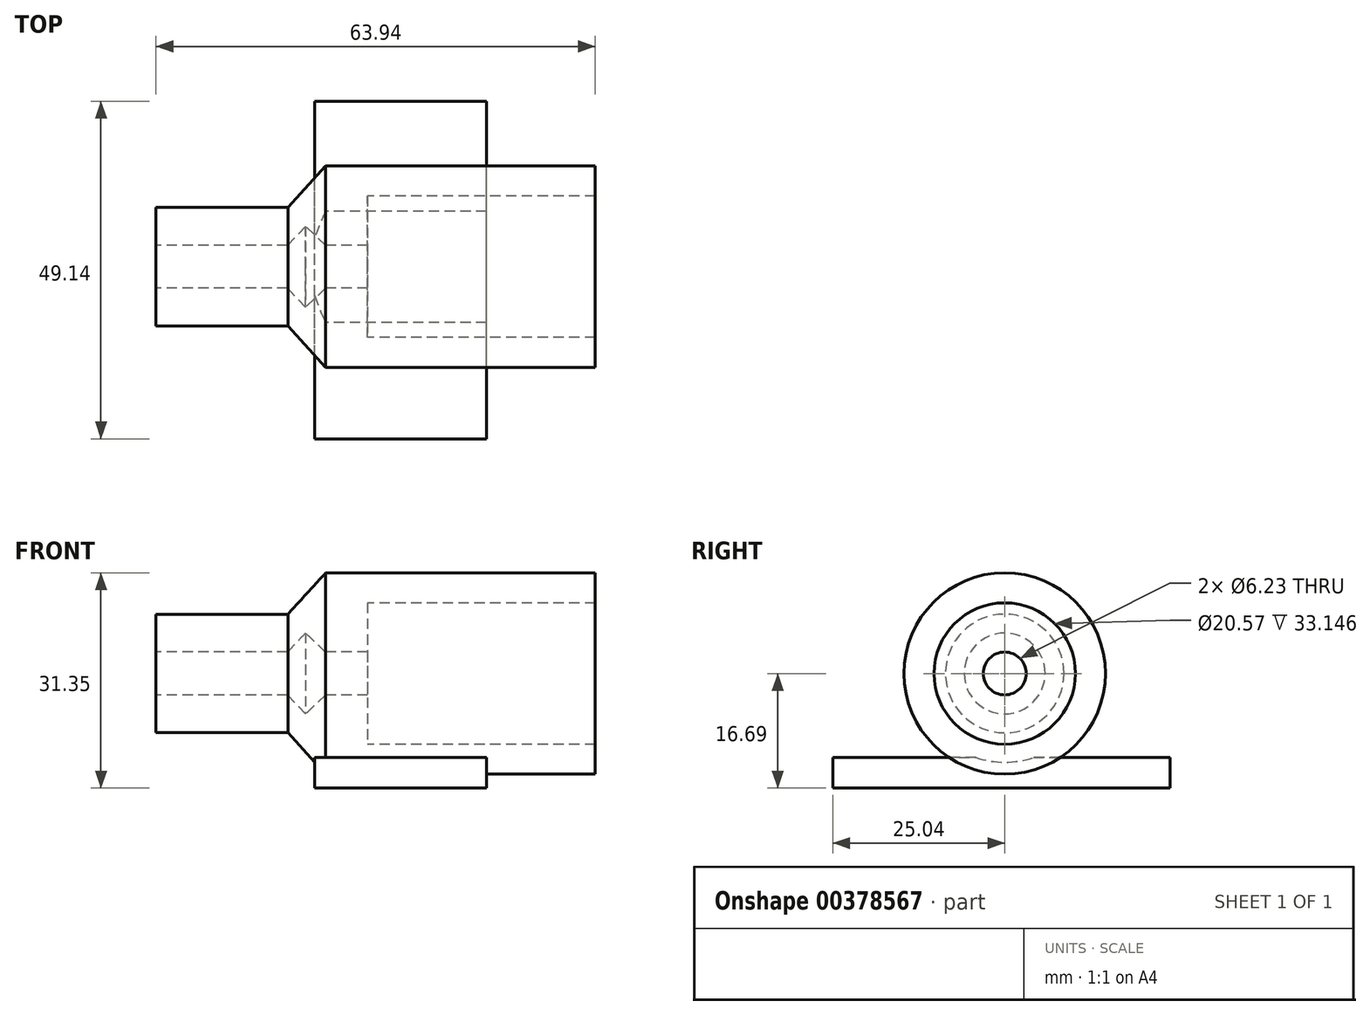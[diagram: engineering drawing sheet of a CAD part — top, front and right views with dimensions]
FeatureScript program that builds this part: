
annotation { "Feature Type Name" : "Feature", "Feature Type Description" : "" }
export const myFeature = defineFeature(function(context is Context, id is Id, definition is map)
    precondition{}
    {
        {
            var Q0;
            Q0=qCreatedBy(makeId("Top.planeOp"),FACE);
            var sketch = newSketch(context, id + "F0", { "sketchPlane" : qUnion([Q0])});
            skLineSegment(sketch, "E0", {"start": v(-35.61, 3.12) * mm, "end": v(-16.46, 3.12) * mm});
            skLineSegment(sketch, "E1", {"start": v(-16.46, 3.12) * mm, "end": v(-13.85, 5.89) * mm});
            skLineSegment(sketch, "E2", {"start": v(-13.85, 5.89) * mm, "end": v(-10.9, 3.12) * mm});
            skLineSegment(sketch, "E3", {"start": v(-10.9, 3.12) * mm, "end": v(-4.82, 3.12) * mm});
            skLineSegment(sketch, "E4", {"start": v(-4.82, 3.12) * mm, "end": v(-4.82, 10.29) * mm});
            skLineSegment(sketch, "E5", {"start": v(-4.82, 10.29) * mm, "end": v(28.33, 10.29) * mm});
            skLineSegment(sketch, "E6", {"start": v(28.33, 10.29) * mm, "end": v(28.33, 14.66) * mm});
            skLineSegment(sketch, "E7", {"start": v(28.33, 14.66) * mm, "end": v(-10.9, 14.66) * mm});
            skLineSegment(sketch, "E8", {"start": v(-10.9, 14.66) * mm, "end": v(-16.42, 8.63) * mm});
            skLineSegment(sketch, "E9", {"start": v(-16.42, 8.63) * mm, "end": v(-35.61, 8.63) * mm});
            skLineSegment(sketch, "E10", {"start": v(-35.61, 8.63) * mm, "end": v(-35.61, 3.12) * mm});
            skLineSegment(sketch, "E11", {"start": v(-42.43, 0) * mm, "end": v(39.38, 0) * mm});
            skSolve(sketch);
        }
        {
            var Q0;
            Q0=makeQuery(id+"F0.imprint","IMPRINT",FACE,{"disambiguationData":[TD([[makeQuery(id+"F0.imprint","IMPRINT",EDGE,{"derivedFrom":sQuery(id+"F0.wireOp",EDGE,"E0")}),1.0]])]});
            var Q1;
            Q1 = qSketchRegion(id + "FOTBG6Bgvnk3PsK_0", true);
            var Q2;
            Q2=sQuery(id+"F0.wireOp",EDGE,"E11");
            revolve(context, id + "F1", {"entities" : qUnion([Q0, Q1]), "axis" : qUnion([Q2]), "revolveType" : RevolveType.FULL});
        }
        {
            var Q0;
            Q0=qCreatedBy(makeId("Right.planeOp"),FACE);
            var sketch = newSketch(context, id + "F2", { "sketchPlane" : qUnion([Q0])});
            skLineSegment(sketch, "E12.bottom", {"start": v(-25.04, -12.22) * mm, "end": v(24.1, -12.22) * mm});
            skLineSegment(sketch, "E12.top", {"start": v(-25.04, -16.7) * mm, "end": v(24.1, -16.7) * mm});
            skLineSegment(sketch, "E12.left", {"start": v(-25.04, -12.22) * mm, "end": v(-25.04, -16.7) * mm});
            skLineSegment(sketch, "E12.right", {"start": v(24.1, -12.22) * mm, "end": v(24.1, -16.7) * mm});
            skSolve(sketch);
        }
        {
            var Q0;
            Q0=makeQuery(id+"F2.imprint","IMPRINT",FACE,{"disambiguationData":[TD([[makeQuery(id+"F2.imprint","IMPRINT",EDGE,{"derivedFrom":sQuery(id+"F2.wireOp",EDGE,"E12.bottom")}),-1.0]])]});
            extrude(context, id + "F3", {"entities" : qUnion([Q0]), "operationType" : NewBodyOperationType.ADD, "endBound" : BoundingType.SYMMETRIC, "depth" : 25 * mm});
        }
    });
